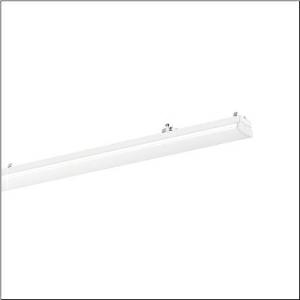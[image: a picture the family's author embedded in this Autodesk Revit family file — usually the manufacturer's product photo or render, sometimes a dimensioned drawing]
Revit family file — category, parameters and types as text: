
# Revit family: licross_11_recessed_opal_mo_51te1d7n44xg
name_source: partatom
category: Lighting Fixtures
units: mm (PartAtom-declared; Revit-internal decimal feet)

## family parameters
Cut with Voids When Loaded = No
Host = Face
Light Source = No
Part Type = Normal
Room Calculation Point = No
Round Connector Dimension = Use Diameter
Shared = No

## types (1)
- Licross 11 recessed opal MO (1 x LED, 4480 lm, 24.8 W, 4000K)
    Apparent Load = 25 VA
    CIE Flux Codes = 44 73 91 87 100
    Color Rendering = 80
    Color Temperature = 4000K
    Default Elevation = 1800 mm
    Description = Licross 11 recessed opal MO, luminaire insert, of sheet steel, coil coated, white, length: 1.500mm, width: 76mm, height: 87mm, LED rated luminous flux: 4.480lm, light colour: 840, SDCM (Standard Deviation of Colour Matching)MacAdam ≤ 2 SDCM (initial), control gear: ON/OFF, with plug, 3-pole, with phase selection, mains connection: 220..240V, AC, 50/60Hz, rated input power: 25W, internal wiring halogen-free, primary optical cover: cover, of PMMA, light emission: direct with ceiling illumination distribution, primary light characteristic: symmetric, protection rating (complete): IP54, insulation class (complete): insulation class I (protective earthing), certification: CE, ENEC, VDE, UKCA, protection symbol: D if used in an environment with non-conductive dust loads with corresponding accessories, impact resistance: IK06, permissible ambient temperature for indoor applications: -35..+45°C, corresponds to IFS (International Featured Standards) requirements for safety and quality in the food industry, reducing of maximum allowable ambient temperature of 5°C with ceiling mounting, The light source and the operating device comply with the requirements of the Ecodesign Regulation (EU) 2019/2020 and are replaceable in accordance with this regulation, packaging unit: 1 piece
    Height = 83 mm
    Lamp = 1 x LED
    Lamp Light Flux = 4480 lm
    Lamp Power = 24.8 W
    Lamp count = 1
    Length = 1500 mm
    Luminous efficacy = 181 lm/W
    Manufacturer = Siteco
    ModVariant = No
    Model = 51TE1D7N44XG
    Mounting Place = Ceiling
    Mounting Type = Pendant
    Number of Poles = 1
    OnlyDefault = Yes
    Power Factor = 1
    Product Name = Licross 11 recessed opal MO
    Product group = luminaire insert | ceiling pendant
    ProductGroupID = 901
    Protection Class = Protection class I
    Protection Degree = IP 54
    RLX_Detail_Level = 1
    RLX_Emergency_Light_Flux = 0 lm
    RLX_Emergency_Type = 0
    RLX_Emergency_Type_DB = No
    RlxData = <blob elided: 23249 chars, md5=f8effd40>
    Socket = socket
    Standby Power = 0 W
    System Light Flux = 4480 lm
    System Power = 25 W
    Type Comments = Product without accessories
    Type Image = l_1313666.jpg
    URL = http://relux.com
    VarID = ---
    Voltage = 0 V
    Weight = 0.00 kg
    Width = 76 mm

## geometry (parser evidence)
native form markers: Blend x4, Sweep x12
no freeform markers — native parametric forms only
